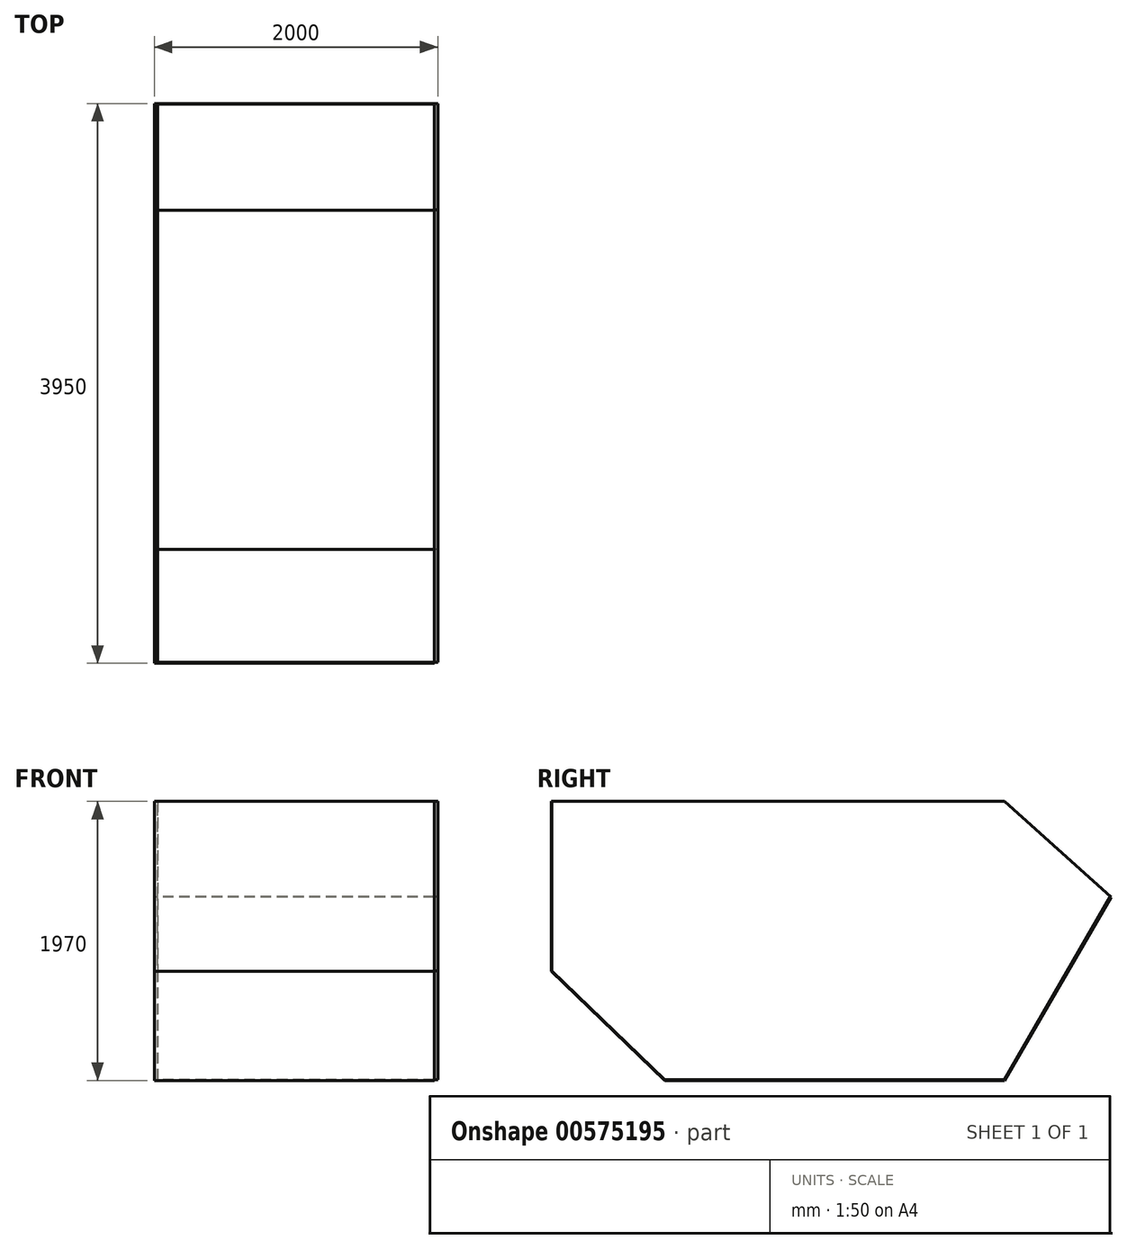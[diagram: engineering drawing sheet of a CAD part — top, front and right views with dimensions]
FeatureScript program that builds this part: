
annotation { "Feature Type Name" : "Feature", "Feature Type Description" : "" }
export const myFeature = defineFeature(function(context is Context, id is Id, definition is map)
    precondition{}
    {
        {
            var Q0;
            Q0=qCreatedBy(makeId("Right.planeOp"),FACE);
            var sketch = newSketch(context, id + "F0", { "sketchPlane" : qUnion([Q0])});
            skLineSegment(sketch, "E0", {"start": v(0, 0) * mm, "end": v(0, -1200) * mm});
            skLineSegment(sketch, "E1", {"start": v(0, -1200) * mm, "end": v(800, -1970) * mm});
            skLineSegment(sketch, "E2", {"start": v(800, -1970) * mm, "end": v(3200, -1970) * mm});
            skLineSegment(sketch, "E3", {"start": v(3200, -1970) * mm, "end": v(3950, -676.22) * mm});
            skLineSegment(sketch, "E4", {"start": v(3950, -676.22) * mm, "end": v(3200, 0) * mm});
            skLineSegment(sketch, "E5", {"start": v(3200, 0) * mm, "end": v(0, 0) * mm});
            skSolve(sketch);
        }
        {
            var Q0;
            Q0=makeQuery(id+"F0.imprint","IMPRINT",FACE,{"disambiguationData":[TD([[makeQuery(id+"F0.imprint","IMPRINT",EDGE,{"derivedFrom":sQuery(id+"F0.wireOp",EDGE,"E0")}),1.0]])]});
            extrude(context, id + "F1", {"entities" : qUnion([Q0]), "depth" : 25 * mm, "offsetDistance" : 25 * mm});
        }
        {
            var Q0;
            Q0=makeQuery(id+"F1.opExtrude","CAP_FACE",FACE,{"disambiguationData":[OSD([sQuery(id+"F0.wireOp",EDGE,"E0"),sQuery(id+"F0.wireOp",EDGE,"E1"),sQuery(id+"F0.wireOp",EDGE,"E2"),sQuery(id+"F0.wireOp",EDGE,"E3"),sQuery(id+"F0.wireOp",EDGE,"E4"),sQuery(id+"F0.wireOp",EDGE,"E5")])],"isStart":false});
            var sketch = newSketch(context, id + "F2", { "sketchPlane" : qUnion([Q0])});
            skLineSegment(sketch, "E6.0", {"start": v(3197.12, -1965) * mm, "end": v(3945.67, -673.72) * mm});
            skLineSegment(sketch, "E6.1", {"start": v(802.02, -1965) * mm, "end": v(3197.12, -1965) * mm});
            skLineSegment(sketch, "E6.2", {"start": v(5, -1197.87) * mm, "end": v(802.02, -1965) * mm});
            skLineSegment(sketch, "E6.3", {"start": v(5, 0) * mm, "end": v(5, -1197.87) * mm});
            skLineSegment(sketch, "E7", {"start": v(5, 0) * mm, "end": v(0, 0) * mm});
            skLineSegment(sketch, "E8", {"start": v(0, 0) * mm, "end": v(0, -1200) * mm});
            skLineSegment(sketch, "E9", {"start": v(0, -1200) * mm, "end": v(800, -1970) * mm});
            skLineSegment(sketch, "E10", {"start": v(800, -1970) * mm, "end": v(3200, -1970) * mm});
            skLineSegment(sketch, "E11", {"start": v(3200, -1970) * mm, "end": v(3950, -676.22) * mm});
            skLineSegment(sketch, "E12", {"start": v(3950, -676.22) * mm, "end": v(3945.67, -673.72) * mm});
            skSolve(sketch);
        }
        {
            var Q0;
            Q0=makeQuery(id+"F2.imprint","IMPRINT",FACE,{"disambiguationData":[TD([[makeQuery(id+"F2.imprint","IMPRINT",EDGE,{"derivedFrom":sQuery(id+"F2.wireOp",EDGE,"E6.0")}),-1.0]])]});
            extrude(context, id + "F3", {"entities" : qUnion([Q0]), "operationType" : NewBodyOperationType.ADD, "depth" : 1950 * mm, "offsetDistance" : 25 * mm});
        }
        {
            var Q0;
            Q0=makeQuery(id+"F3.opExtrude","CAP_FACE",FACE,{"disambiguationData":[OSD([sQuery(id+"F2.wireOp",EDGE,"E6.0"),sQuery(id+"F2.wireOp",EDGE,"E6.1"),sQuery(id+"F2.wireOp",EDGE,"E6.2"),sQuery(id+"F2.wireOp",EDGE,"E6.3"),sQuery(id+"F2.wireOp",EDGE,"E7"),sQuery(id+"F2.wireOp",EDGE,"E8"),sQuery(id+"F2.wireOp",EDGE,"E9"),sQuery(id+"F2.wireOp",EDGE,"E10"),sQuery(id+"F2.wireOp",EDGE,"E11"),sQuery(id+"F2.wireOp",EDGE,"E12")])],"isStart":false});
            var sketch = newSketch(context, id + "F4", { "sketchPlane" : qUnion([Q0])});
            skLineSegment(sketch, "E13.0", {"start": v(3200, 0) * mm, "end": v(5, 0) * mm});
            skLineSegment(sketch, "E14.0", {"start": v(3950, -676.22) * mm, "end": v(3200, 0) * mm});
            skLineSegment(sketch, "E15.0", {"start": v(3200, -1970) * mm, "end": v(3950, -676.22) * mm});
            skLineSegment(sketch, "E16.0", {"start": v(800, -1970) * mm, "end": v(3200, -1970) * mm});
            skLineSegment(sketch, "E17.0", {"start": v(0, -1200) * mm, "end": v(800, -1970) * mm});
            skLineSegment(sketch, "E18.0", {"start": v(0, 0) * mm, "end": v(0, -1200) * mm});
            skSolve(sketch);
        }
        {
            var Q0;
            Q0=makeQuery(id+"F4.imprint","IMPRINT",FACE,{"disambiguationData":[TD([[makeQuery(id+"F4.imprint","IMPRINT",EDGE,{"derivedFrom":sQuery(id+"F4.wireOp",EDGE,"E13.0")}),1.0]])]});
            extrude(context, id + "F5", {"entities" : qUnion([Q0]), "depth" : 25 * mm, "offsetDistance" : 25 * mm});
        }
    });
